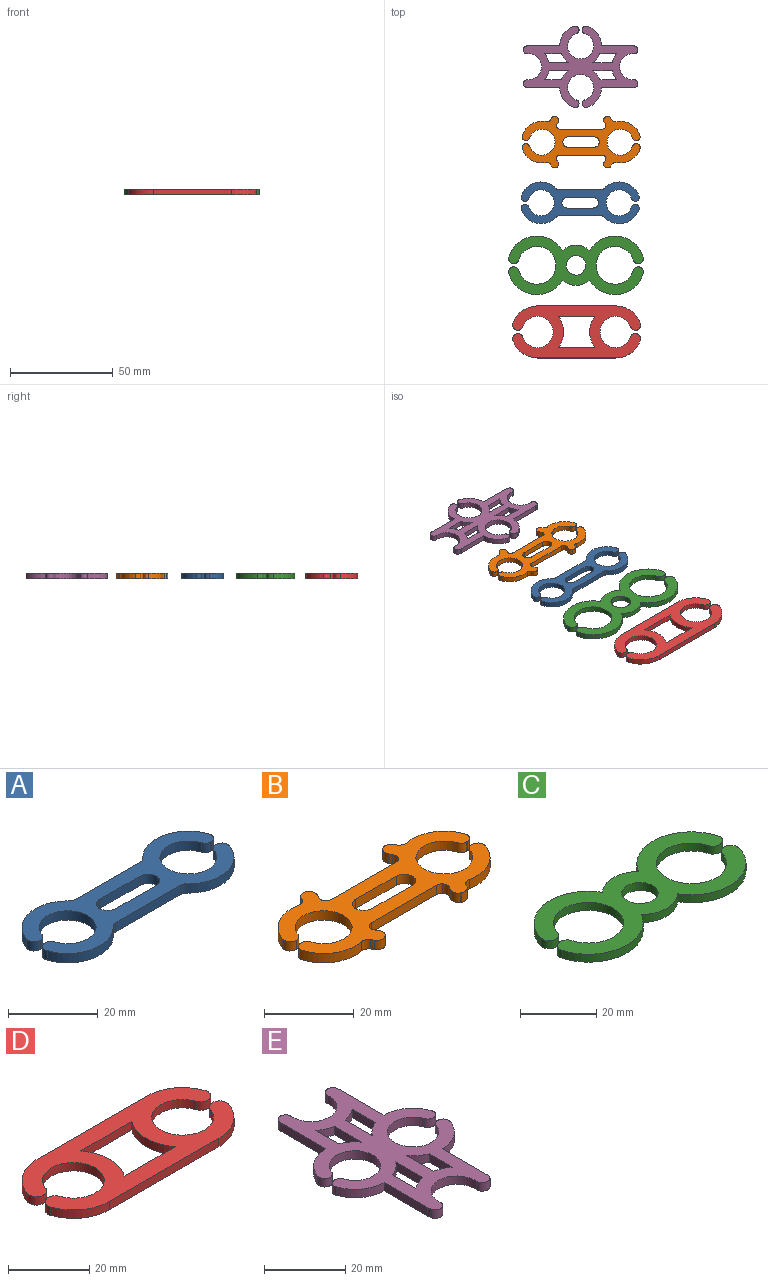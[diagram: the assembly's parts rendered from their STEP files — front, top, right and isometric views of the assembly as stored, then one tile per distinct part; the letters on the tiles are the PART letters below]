
ASSEMBLY  parts=5 mates=5
PART A: 30 faces, bbox 57.6x20.3x2.5 mm
  f0: plane 57.58x20.32mm, normal (0,0,1), area 536.5mm2, adj f2,f3,f4,f5,f6,f7,f8,f9
  f1: plane 57.58x20.32mm, normal (0,0,-1), area 536.5mm2, adj f2,f3,f4,f5,f6,f7,f8,f9
  f2: cylinder r=10.16mm len=17.08mm, axis (0,0,-1), area 53.5mm2, adj f0,f1,f18,f22
  f3: cylinder r=10.16mm len=17.08mm, axis (0,0,-1), area 53.5mm2, adj f0,f1,f15,f25
  f4: cylinder r=6.35mm len=12.7mm, axis (0,0,1), area 90.9mm2, adj f0,f1,f20,f21
  f5: cylinder r=10.16mm len=17.08mm, axis (0,0,-1), area 53.5mm2, adj f0,f1,f19,f23
  f6: plane 20.56x2.54mm, normal (0,-1,0), area 52.2mm2, adj f0,f1,f23,f25
  f7: cylinder r=10.16mm len=17.08mm, axis (0,0,-1), area 53.5mm2, adj f0,f1,f14,f24
  f8: plane 20.56x2.54mm, normal (0,1,0), area 52.2mm2, adj f0,f1,f22,f24
  f9: cylinder r=6.35mm len=12.7mm, axis (0,0,1), area 90.9mm2, adj f0,f1,f16,f17
  f10: plane 2.54x0.13mm, normal (0,1,0), area 0.3mm2, adj f0,f1,f19,f21
  f11: plane 2.54x0.13mm, normal (0,-1,0), area 0.3mm2, adj f0,f1,f18,f20
  f12: plane 2.54x0.13mm, normal (0,1,0), area 0.3mm2, adj f0,f1,f15,f17
  f13: plane 2.54x0.13mm, normal (0,-1,0), area 0.3mm2, adj f0,f1,f14,f16
  f14: cylinder r=1.84mm len=2.54mm, axis (0,0,-1), area 8.8mm2, adj f0,f1,f7,f13
  f15: cylinder r=1.84mm len=2.54mm, axis (0,0,-1), area 8.8mm2, adj f0,f1,f3,f12
  f16: cylinder r=1.84mm len=2.54mm, axis (0,0,1), area 5.8mm2, adj f0,f1,f9,f13
  f17: cylinder r=1.84mm len=2.54mm, axis (0,0,1), area 5.8mm2, adj f0,f1,f9,f12
  f18: cylinder r=1.84mm len=2.54mm, axis (0,0,-1), area 8.8mm2, adj f0,f1,f2,f11
  f19: cylinder r=1.84mm len=2.54mm, axis (0,0,-1), area 8.8mm2, adj f0,f1,f5,f10
  f20: cylinder r=1.84mm len=2.54mm, axis (0,0,1), area 5.8mm2, adj f0,f1,f4,f11
  f21: cylinder r=1.84mm len=2.54mm, axis (0,0,1), area 5.8mm2, adj f0,f1,f4,f10
  f22: cylinder r=1.84mm len=2.54mm, axis (0,0,-1), area 3.8mm2, adj f0,f1,f2,f8
  f23: cylinder r=1.84mm len=2.54mm, axis (0,0,-1), area 3.8mm2, adj f0,f1,f5,f6
  f24: cylinder r=1.84mm len=2.54mm, axis (0,0,-1), area 3.8mm2, adj f0,f1,f7,f8
  f25: cylinder r=1.84mm len=2.54mm, axis (0,0,-1), area 3.8mm2, adj f0,f1,f3,f6
  f26: plane 12.7x2.54mm, normal (0,-1,0), area 32.3mm2, adj f0,f1,f28,f29
  f27: plane 12.7x2.54mm, normal (0,1,0), area 32.3mm2, adj f0,f1,f28,f29
  f28: cylinder r=2.54mm len=5.08mm, axis (0,0,1), area 20.3mm2, adj f0,f1,f26,f27
  f29: cylinder r=2.54mm len=5.08mm, axis (0,0,1), area 20.3mm2, adj f0,f1,f26,f27
PART B: 58 faces, bbox 57.6x25.1x2.5 mm
  f0: cylinder r=10.16mm len=11.73mm, axis (0,0,-1), area 37.6mm2, adj f2,f3,f30,f51
  f1: cylinder r=10.16mm len=11.73mm, axis (0,0,-1), area 37.6mm2, adj f2,f3,f41,f54
  f2: plane 57.58x25.13mm, normal (0,0,1), area 595.9mm2, adj f0,f1,f4,f5,f6,f7,f8,f9
  f3: plane 57.58x25.13mm, normal (0,0,-1), area 595.9mm2, adj f0,f1,f4,f5,f6,f7,f8,f9
  f4: cylinder r=6.35mm len=12.7mm, axis (0,0,1), area 90.9mm2, adj f2,f3,f56,f57
  f5: cylinder r=10.16mm len=11.73mm, axis (0,0,-1), area 37.6mm2, adj f2,f3,f35,f55
  f6: plane 20.56x2.54mm, normal (0,-1,0), area 52.2mm2, adj f2,f3,f31,f33
  f7: cylinder r=10.16mm len=11.73mm, axis (0,0,-1), area 37.6mm2, adj f2,f3,f38,f50
  f8: plane 20.56x2.54mm, normal (0,1,0), area 52.2mm2, adj f2,f3,f36,f39
  f9: cylinder r=6.35mm len=12.7mm, axis (0,0,1), area 90.9mm2, adj f2,f3,f52,f53
  f10: plane 2.54x0.13mm, normal (0,1,0), area 0.3mm2, adj f2,f3,f55,f57
  f11: plane 2.54x0.13mm, normal (0,-1,0), area 0.3mm2, adj f2,f3,f54,f56
  f12: plane 2.54x0.13mm, normal (0,1,0), area 0.3mm2, adj f2,f3,f51,f53
  f13: plane 2.54x0.13mm, normal (0,-1,0), area 0.3mm2, adj f2,f3,f50,f52
  f14: plane 12.7x2.54mm, normal (0,-1,0), area 32.3mm2, adj f2,f3,f16,f17
  f15: plane 12.7x2.54mm, normal (0,1,0), area 32.3mm2, adj f2,f3,f16,f17
  f16: cylinder r=2.54mm len=5.08mm, axis (0,0,1), area 20.3mm2, adj f2,f3,f14,f15
  f17: cylinder r=2.54mm len=5.08mm, axis (0,0,1), area 20.3mm2, adj f2,f3,f14,f15
  f18: plane 2.54x0.82mm, normal (0.87,-0.5,0), area 2.4mm2, adj f2,f3,f40,f48
  f19: plane 2.54x0.82mm, normal (-0.87,0.5,0), area 2.4mm2, adj f2,f3,f41,f49
  f20: plane 2.54x0.11mm, normal (0.5,0.87,0), area 0.3mm2, adj f2,f3,f48,f49
  f21: plane 2.54x0.82mm, normal (-0.87,-0.5,0), area 2.4mm2, adj f2,f3,f37,f46
  f22: plane 2.54x0.82mm, normal (0.87,0.5,0), area 2.4mm2, adj f2,f3,f38,f47
  f23: plane 2.54x0.11mm, normal (-0.5,0.87,0), area 0.3mm2, adj f2,f3,f46,f47
  f24: plane 2.54x0.82mm, normal (0.87,0.5,0), area 2.4mm2, adj f2,f3,f34,f44
  f25: plane 2.54x0.82mm, normal (-0.87,-0.5,0), area 2.4mm2, adj f2,f3,f35,f45
  f26: plane 2.54x0.11mm, normal (0.5,-0.87,0), area 0.3mm2, adj f2,f3,f44,f45
  f27: plane 2.54x0.82mm, normal (0.87,-0.5,0), area 2.4mm2, adj f2,f3,f30,f42
  f28: plane 2.54x0.82mm, normal (-0.87,0.5,0), area 2.4mm2, adj f2,f3,f32,f43
  f29: plane 2.54x0.11mm, normal (-0.5,-0.87,0), area 0.3mm2, adj f2,f3,f42,f43
  f30: cylinder r=1.84mm len=2.54mm, axis (0,0,-1), area 5.9mm2, adj f0,f2,f3,f27
  f31: cylinder r=1.84mm len=2.54mm, axis (0,0,-1), area 3.6mm2, adj f2,f3,f6,f32
  f32: cylinder r=1.84mm len=2.54mm, axis (0,0,-1), area 5.6mm2, adj f2,f3,f28,f31
  f33: cylinder r=1.84mm len=2.54mm, axis (0,0,-1), area 3.6mm2, adj f2,f3,f6,f34
  f34: cylinder r=1.84mm len=2.54mm, axis (0,0,-1), area 5.6mm2, adj f2,f3,f24,f33
  f35: cylinder r=1.84mm len=2.54mm, axis (0,0,-1), area 5.9mm2, adj f2,f3,f5,f25
  f36: cylinder r=1.84mm len=2.54mm, axis (0,0,-1), area 3.6mm2, adj f2,f3,f8,f37
  f37: cylinder r=1.84mm len=2.54mm, axis (0,0,-1), area 5.6mm2, adj f2,f3,f21,f36
  f38: cylinder r=1.84mm len=2.54mm, axis (0,0,-1), area 5.9mm2, adj f2,f3,f7,f22
  f39: cylinder r=1.84mm len=2.54mm, axis (0,0,-1), area 3.6mm2, adj f2,f3,f8,f40
  f40: cylinder r=1.84mm len=2.54mm, axis (0,0,-1), area 5.6mm2, adj f2,f3,f18,f39
  f41: cylinder r=1.84mm len=2.54mm, axis (0,0,-1), area 5.9mm2, adj f1,f2,f3,f19
  f42: cylinder r=1.84mm len=2.54mm, axis (0,0,1), area 7.3mm2, adj f2,f3,f27,f29
  f43: cylinder r=1.84mm len=2.54mm, axis (0,0,1), area 7.3mm2, adj f2,f3,f28,f29
  f44: cylinder r=1.84mm len=2.54mm, axis (0,0,1), area 7.3mm2, adj f2,f3,f24,f26
  f45: cylinder r=1.84mm len=2.54mm, axis (0,0,1), area 7.3mm2, adj f2,f3,f25,f26
  f46: cylinder r=1.84mm len=2.54mm, axis (0,0,1), area 7.3mm2, adj f2,f3,f21,f23
  f47: cylinder r=1.84mm len=2.54mm, axis (0,0,1), area 7.3mm2, adj f2,f3,f22,f23
  f48: cylinder r=1.84mm len=2.54mm, axis (0,0,1), area 7.3mm2, adj f2,f3,f18,f20
  f49: cylinder r=1.84mm len=2.54mm, axis (0,0,1), area 7.3mm2, adj f2,f3,f19,f20
  f50: cylinder r=1.84mm len=2.54mm, axis (0,0,-1), area 8.8mm2, adj f2,f3,f7,f13
  f51: cylinder r=1.84mm len=2.54mm, axis (0,0,-1), area 8.8mm2, adj f0,f2,f3,f12
  f52: cylinder r=1.84mm len=2.54mm, axis (0,0,1), area 5.8mm2, adj f2,f3,f9,f13
  f53: cylinder r=1.84mm len=2.54mm, axis (0,0,1), area 5.8mm2, adj f2,f3,f9,f12
  f54: cylinder r=1.84mm len=2.54mm, axis (0,0,-1), area 8.8mm2, adj f1,f2,f3,f11
  f55: cylinder r=1.84mm len=2.54mm, axis (0,0,-1), area 8.8mm2, adj f2,f3,f5,f10
  f56: cylinder r=1.84mm len=2.54mm, axis (0,0,1), area 5.8mm2, adj f2,f3,f4,f11
  f57: cylinder r=1.84mm len=2.54mm, axis (0,0,1), area 5.8mm2, adj f2,f3,f4,f10
PART C: 15 faces, bbox 65.7x28.6x2.5 mm
  f0: cylinder r=14.29mm len=26.05mm, axis (0,0,-1), area 84.5mm2, adj f2,f3,f8,f13
  f1: cylinder r=14.29mm len=26.05mm, axis (0,0,-1), area 84.5mm2, adj f2,f3,f6,f12
  f2: plane 65.73x28.58mm, normal (0,0,1), area 855.2mm2, adj f0,f1,f4,f5,f6,f7,f8,f9
  f3: plane 65.73x28.58mm, normal (0,0,-1), area 855.2mm2, adj f0,f1,f4,f5,f6,f7,f8,f9
  f4: cylinder r=9.21mm len=18.42mm, axis (0,0,1), area 133.6mm2, adj f2,f3,f13,f14
  f5: cylinder r=14.29mm len=26.05mm, axis (0,0,-1), area 84.5mm2, adj f2,f3,f6,f14
  f6: cylinder r=9.84mm len=13.42mm, axis (0,0,-1), area 37.5mm2, adj f1,f2,f3,f5
  f7: cylinder r=14.29mm len=26.05mm, axis (0,0,-1), area 84.5mm2, adj f2,f3,f8,f11
  f8: cylinder r=9.84mm len=13.42mm, axis (0,0,-1), area 37.5mm2, adj f0,f2,f3,f7
  f9: cylinder r=4.76mm len=9.53mm, axis (0,0,1), area 76mm2, adj f2,f3
  f10: cylinder r=9.21mm len=18.42mm, axis (0,0,1), area 133.6mm2, adj f2,f3,f11,f12
  f11: cylinder r=2.54mm len=4.98mm, axis (0,0,1), area 20.3mm2, adj f2,f3,f7,f10
  f12: cylinder r=2.54mm len=4.98mm, axis (0,0,1), area 20.3mm2, adj f1,f2,f3,f10
  f13: cylinder r=2.54mm len=4.98mm, axis (0,0,1), area 20.3mm2, adj f0,f2,f3,f4
  f14: cylinder r=2.54mm len=4.98mm, axis (0,0,1), area 20.3mm2, adj f2,f3,f4,f5
PART D: 18 faces, bbox 62.4x25.4x2.5 mm
  f0: plane 62.4x25.4mm, normal (0,0,1), area 863.6mm2, adj f2,f3,f4,f5,f6,f7,f8,f9
  f1: plane 62.4x25.4mm, normal (0,0,-1), area 863.6mm2, adj f2,f3,f4,f5,f6,f7,f8,f9
  f2: cylinder r=12.7mm len=12.01mm, axis (0,0,-1), area 40mm2, adj f0,f1,f9,f14
  f3: cylinder r=12.7mm len=12.01mm, axis (0,0,-1), area 40mm2, adj f0,f1,f8,f15
  f4: cylinder r=12.7mm len=12.01mm, axis (0,0,-1), area 40mm2, adj f0,f1,f8,f16
  f5: cylinder r=12.7mm len=12.01mm, axis (0,0,-1), area 40mm2, adj f0,f1,f9,f17
  f6: cylinder r=7.62mm len=15.24mm, axis (0,0,1), area 108.8mm2, adj f0,f1,f14,f15
  f7: cylinder r=7.62mm len=15.24mm, axis (0,0,1), area 108.8mm2, adj f0,f1,f16,f17
  f8: plane 38.1x2.54mm, normal (0,-1,0), area 96.8mm2, adj f0,f1,f3,f4
  f9: plane 38.1x2.54mm, normal (0,1,0), area 96.8mm2, adj f0,f1,f2,f5
  f10: plane 17.78x2.54mm, normal (0,1,0), area 45.2mm2, adj f0,f1,f11,f13
  f11: cylinder r=12.7mm len=15.24mm, axis (0,0,1), area 41.5mm2, adj f0,f1,f10,f12
  f12: plane 17.78x2.54mm, normal (0,-1,0), area 45.2mm2, adj f0,f1,f11,f13
  f13: cylinder r=12.7mm len=15.24mm, axis (0,0,1), area 41.5mm2, adj f0,f1,f10,f12
  f14: cylinder r=2.54mm len=4.94mm, axis (0,0,1), area 20.3mm2, adj f0,f1,f2,f6
  f15: cylinder r=2.54mm len=4.94mm, axis (0,0,1), area 20.3mm2, adj f0,f1,f3,f6
  f16: cylinder r=2.54mm len=4.94mm, axis (0,0,1), area 20.3mm2, adj f0,f1,f4,f7
  f17: cylinder r=2.54mm len=4.94mm, axis (0,0,1), area 20.3mm2, adj f0,f1,f5,f7
PART E: 42 faces, bbox 39.8x55.9x2.5 mm
  f0: cylinder r=10.16mm len=9.62mm, axis (0,0,-1), area 32mm2, adj f2,f3,f28,f36
  f1: cylinder r=10.16mm len=9.62mm, axis (0,0,-1), area 32mm2, adj f2,f3,f31,f34
  f2: plane 55.88x39.75mm, normal (0,0,1), area 844.4mm2, adj f0,f1,f4,f5,f6,f7,f8,f9
  f3: plane 55.88x39.75mm, normal (0,0,-1), area 844.4mm2, adj f0,f1,f4,f5,f6,f7,f8,f9
  f4: cylinder r=6.35mm len=12.7mm, axis (0,0,1), area 90.7mm2, adj f2,f3,f34,f35
  f5: cylinder r=6.35mm len=12.7mm, axis (0,0,1), area 90.7mm2, adj f2,f3,f36,f37
  f6: cylinder r=10.16mm len=4.45mm, axis (0,0,-1), area 12.6mm2, adj f2,f3,f17,f32
  f7: cylinder r=10.16mm len=9.62mm, axis (0,0,-1), area 32mm2, adj f2,f3,f33,f37
  f8: cylinder r=10.16mm len=4.45mm, axis (0,0,-1), area 14.6mm2, adj f2,f3,f14,f30
  f9: cylinder r=10.16mm len=2.54mm, axis (0,0,-1), area 2mm2, adj f2,f3,f31,f41
  f10: cylinder r=10.16mm len=4.45mm, axis (0,0,-1), area 14.6mm2, adj f2,f3,f19,f29
  f11: cylinder r=10.16mm len=2.54mm, axis (0,0,-1), area 2mm2, adj f2,f3,f28,f38
  f12: cylinder r=10.16mm len=4.45mm, axis (0,0,-1), area 12.6mm2, adj f2,f3,f22,f26
  f13: cylinder r=10.16mm len=9.62mm, axis (0,0,-1), area 32mm2, adj f2,f3,f27,f35
  f14: plane 9.5x2.54mm, normal (1,0,0), area 24.1mm2, adj f2,f3,f8,f15
  f15: cylinder r=10.16mm len=4.45mm, axis (0,0,-1), area 12.6mm2, adj f2,f3,f14,f30
  f16: cylinder r=10.16mm len=2.54mm, axis (0,0,-1), area 2mm2, adj f2,f3,f33,f40
  f17: plane 9.5x2.54mm, normal (-1,0,0), area 24.1mm2, adj f2,f3,f6,f18
  f18: cylinder r=10.16mm len=4.45mm, axis (0,0,-1), area 14.6mm2, adj f2,f3,f17,f32
  f19: plane 9.5x2.54mm, normal (-1,0,0), area 24.1mm2, adj f2,f3,f10,f20
  f20: cylinder r=10.16mm len=4.45mm, axis (0,0,-1), area 12.6mm2, adj f2,f3,f19,f29
  f21: cylinder r=10.16mm len=2.54mm, axis (0,0,-1), area 2mm2, adj f2,f3,f27,f39
  f22: plane 9.5x2.54mm, normal (1,0,0), area 24.1mm2, adj f2,f3,f12,f23
  f23: cylinder r=10.16mm len=4.45mm, axis (0,0,-1), area 14.6mm2, adj f2,f3,f22,f26
  f24: cylinder r=6.35mm len=12.7mm, axis (0,0,1), area 53.2mm2, adj f2,f3,f40,f41
  f25: cylinder r=6.35mm len=12.7mm, axis (0,0,1), area 53.2mm2, adj f2,f3,f38,f39
  f26: plane 8.05x2.54mm, normal (-1,0,0), area 20.4mm2, adj f2,f3,f12,f23
  f27: plane 15.24x2.54mm, normal (1,0,0), area 38.7mm2, adj f2,f3,f13,f21
  f28: plane 15.24x2.54mm, normal (-1,0,0), area 38.7mm2, adj f0,f2,f3,f11
  f29: plane 8.05x2.54mm, normal (1,0,0), area 20.4mm2, adj f2,f3,f10,f20
  f30: plane 8.05x2.54mm, normal (-1,0,0), area 20.4mm2, adj f2,f3,f8,f15
  f31: plane 15.24x2.54mm, normal (1,0,0), area 38.7mm2, adj f1,f2,f3,f9
  f32: plane 8.05x2.54mm, normal (1,0,0), area 20.4mm2, adj f2,f3,f6,f18
  f33: plane 15.24x2.54mm, normal (-1,0,0), area 38.7mm2, adj f2,f3,f7,f16
  f34: cylinder r=1.91mm len=3.71mm, axis (0,0,1), area 15.2mm2, adj f1,f2,f3,f4
  f35: cylinder r=1.91mm len=3.71mm, axis (0,0,1), area 15.2mm2, adj f2,f3,f4,f13
  f36: cylinder r=1.91mm len=3.71mm, axis (0,0,1), area 15.2mm2, adj f0,f2,f3,f5
  f37: cylinder r=1.91mm len=3.71mm, axis (0,0,1), area 15.2mm2, adj f2,f3,f5,f7
  f38: cylinder r=1.91mm len=3.8mm, axis (0,0,-1), area 15.2mm2, adj f2,f3,f11,f25
  f39: cylinder r=1.91mm len=3.8mm, axis (0,0,-1), area 15.2mm2, adj f2,f3,f21,f25
  f40: cylinder r=1.91mm len=3.8mm, axis (0,0,-1), area 15.2mm2, adj f2,f3,f16,f24
  f41: cylinder r=1.91mm len=3.8mm, axis (0,0,-1), area 15.2mm2, adj f2,f3,f9,f24
PLACE A t=(2.55,37.98,-15.23)mm
PLACE B t=(3,67.57,-15.23)mm
PLACE C t=(0.52,7.51,-15.23)mm
PLACE D t=(0.83,-24.96,-15.23)mm fixed
PLACE E rot(axis=(0,0,1),90deg) t=(2.78,104.29,-16.5)mm
MATE planar D.f0 <-> C.f2  axis (0,0,1) through (9.72,-32.58,-13.96)mm
MATE planar E.f2 <-> B.f2  axis (0,0,1) through (-23.1,97.96,-13.96)mm
MATE planar B.f2 <-> A.f0  axis (0,0,1) through (-7.27,61.22,-13.96)mm
MATE parallel D.f9 <-> E.f27  axis (0,1,0) through (0.83,-12.26,-15.23)mm
MATE planar D.f0 <-> A.f0  axis (0,0,1) through (0.83,-24.96,-13.96)mm
